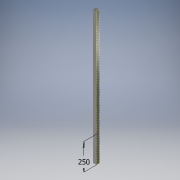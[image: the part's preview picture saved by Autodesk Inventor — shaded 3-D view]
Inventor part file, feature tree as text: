
AUTODESK INVENTOR PART (.ipt)
format: ipt  version: 2019 (Build 230136000, 136)  size: 111,104 bytes
history: native  units: mm
features: sketch x2, extrude x1, projected_geometry x1
ambient origin geometry x8: Origin, YZ Plane, XZ Plane, XY Plane, X Axis, Y Axis, Z Axis, Center Point
bodies: Solid1 (feature_tree)
feature tree (4):
  extrude  "Extrusion1"  Depth=30.0mm
  sketch  "Sketch2"  dims[d2=2.5mm d3=2.5mm d4=1250.0mm d5=0.0mm d6=250.0mm]
  sketch  "Sketch1"  dims[d0=30.0mm d1=30.0mm]
  projected_geometry  "Projected Loop1"
